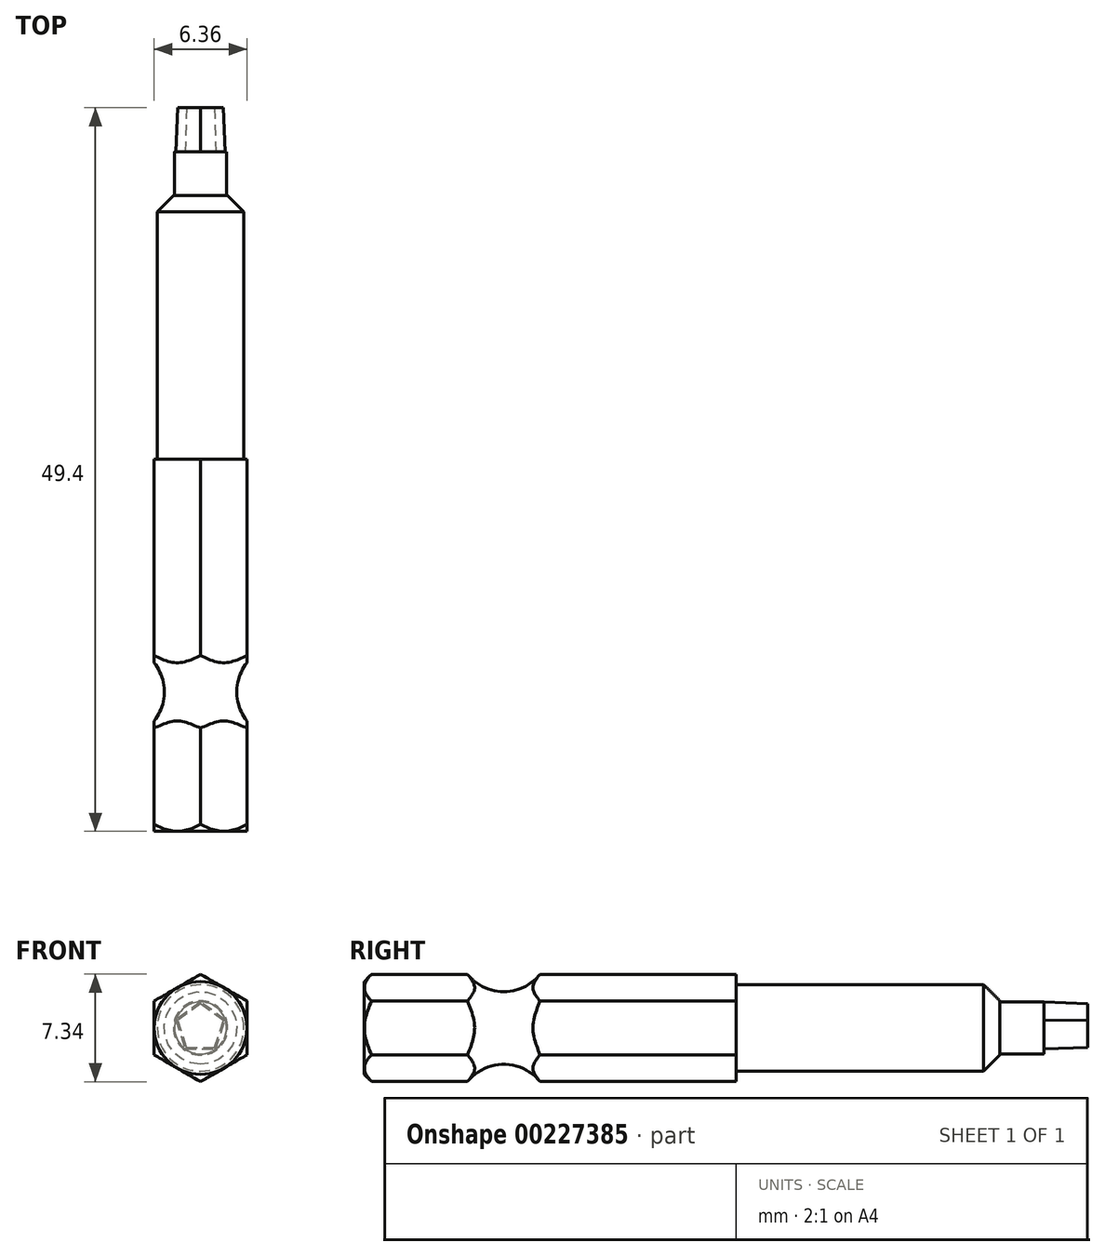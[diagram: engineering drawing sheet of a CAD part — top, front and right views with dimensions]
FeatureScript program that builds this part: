
annotation { "Feature Type Name" : "Feature", "Feature Type Description" : "" }
export const myFeature = defineFeature(function(context is Context, id is Id, definition is map)
    precondition{}
    {
        {
            var Q0;
            Q0=qCreatedBy(makeId("Front.planeOp"),FACE);
            var sketch = newSketch(context, id + "F0", { "sketchPlane" : qUnion([Q0])});
            skCircle(sketch, "E0.cCircle", {"center": v(0, 0) * mm, "radius": 3.17 * mm, "construction": true});
            skLineSegment(sketch, "E0.0", {"start": v(0, 3.67) * mm, "end": v(3.18, 1.83) * mm});
            skLineSegment(sketch, "E0.1", {"start": v(3.17, 1.83) * mm, "end": v(3.17, -1.83) * mm});
            skLineSegment(sketch, "E0.2", {"start": v(3.18, -1.83) * mm, "end": v(0, -3.67) * mm});
            skLineSegment(sketch, "E0.3", {"start": v(0, -3.67) * mm, "end": v(-3.17, -1.83) * mm});
            skLineSegment(sketch, "E0.4", {"start": v(-3.17, -1.83) * mm, "end": v(-3.17, 1.83) * mm});
            skLineSegment(sketch, "E0.5", {"start": v(-3.17, 1.83) * mm, "end": v(0, 3.67) * mm});
            skPoint(sketch, "E0.0.midPoint", {"position": v(1.59, 2.75) * mm});
            skSolve(sketch);
        }
        {
            var Q0;
            Q0=qSketchRegion(id+"F0",true);
            extrude(context, id + "F1", {"entities" : qUnion([Q0]), "oppositeDirection" : true, "depth" : 25.4 * mm});
        }
        {
            var Q0;
            Q0=qCreatedBy(makeId("Right.planeOp"),FACE);
            var sketch = newSketch(context, id + "F2", { "sketchPlane" : qUnion([Q0])});
            skLineSegment(sketch, "E1", {"start": v(0, 0) * mm, "end": v(2.72, 0) * mm});
            skSolve(sketch);
        }
        {
            var Q0;
            Q0=qCreatedBy(makeId("Right.planeOp"),FACE);
            var sketch = newSketch(context, id + "F3", { "sketchPlane" : qUnion([Q0])});
            skLineSegment(sketch, "E2", {"start": v(0, 3.67) * mm, "end": v(0.5, 3.67) * mm});
            skLineSegment(sketch, "E3", {"start": v(0.5, 3.67) * mm, "end": v(0, 3.17) * mm});
            skLineSegment(sketch, "E4", {"start": v(0, 3.17) * mm, "end": v(0, 3.67) * mm});
            skSolve(sketch);
        }
        {
            var Q0;
            Q0=qSketchRegion(id+"F3",true);
            var Q1;
            Q1=sQuery(id+"F2.wireOp",EDGE,"E1");
            revolve(context, id + "F4", {"operationType" : NewBodyOperationType.REMOVE, "entities" : qUnion([Q0]), "axis" : qUnion([Q1]), "revolveType" : RevolveType.FULL, "oppositeDirection" : true});
        }
        {
            var Q0;
            Q0=makeQuery(id+"F1.opExtrude","SWEPT_FACE",FACE,{"disambiguationData":[OSD([sQuery(id+"F0.wireOp",EDGE,"E0.0")])]});
            var sketch = newSketch(context, id + "F5", { "sketchPlane" : qUnion([Q0])});
            skPoint(sketch, "E5", {"position": v(0, 25.4) * mm});
            skSolve(sketch);
        }
        {
            var Q0;
            Q0=makeQuery(id+"F1.opExtrude","CAP_EDGE",EDGE,{"disambiguationData":[OSD([sQuery(id+"F0.wireOp",EDGE,"E0.0")])],"isStart":false});
            var Q1;
            Q1=sQuery(id+"F2.wireOp",VERTEX,"E1.start");
            cPlane(context, id + "F6", {"entities" : qUnion([Q0, Q1]), "cplaneType" : CPlaneType.LINE_POINT, "offset" : 150 * mm, "width" : 150 * mm, "height" : 150 * mm});
        }
        {
            var Q0;
            Q0=qCreatedBy(id+"F6.planeOp",FACE);
            var sketch = newSketch(context, id + "F7", { "sketchPlane" : qUnion([Q0])});
            skArc(sketch, "E6", {"start": v(6.41, 5.03) * mm, "mid": v(9.53, 2.48) * mm, "end": v(12.64, 5.03) * mm});
            skLineSegment(sketch, "E7", {"start": v(6.41, 5.03) * mm, "end": v(12.64, 5.03) * mm});
            skPoint(sketch, "E8", {"position": v(9.53, 2.48) * mm});
            skSolve(sketch);
        }
        {
            var Q0;
            Q0=qSketchRegion(id+"F7",true);
            var Q1;
            Q1=sQuery(id+"F2.wireOp",EDGE,"E1");
            revolve(context, id + "F8", {"operationType" : NewBodyOperationType.REMOVE, "entities" : qUnion([Q0]), "axis" : qUnion([Q1]), "revolveType" : RevolveType.FULL});
        }
        {
            var Q0;
            Q0=makeQuery(id+"F1.opExtrude","CAP_FACE",FACE,{"disambiguationData":[OSD([sQuery(id+"F0.wireOp",EDGE,"E0.0"),sQuery(id+"F0.wireOp",EDGE,"E0.1"),sQuery(id+"F0.wireOp",EDGE,"E0.2"),sQuery(id+"F0.wireOp",EDGE,"E0.3"),sQuery(id+"F0.wireOp",EDGE,"E0.4"),sQuery(id+"F0.wireOp",EDGE,"E0.5")])],"isStart":false});
            var sketch = newSketch(context, id + "F9", { "sketchPlane" : qUnion([Q0])});
            skCircle(sketch, "E9", {"center": v(0, 0) * mm, "radius": 2.95 * mm});
            skSolve(sketch);
        }
        {
            var Q0;
            Q0 = qSketchRegion(id + "F9", true);
            extrude(context, id + "F10", {"entities" : qUnion([Q0]), "operationType" : NewBodyOperationType.ADD, "depth" : 18 * mm, "offsetDistance" : 25 * mm});
        }
        {
            var Q0;
            Q0=makeQuery(id+"F10.opExtrude","CAP_FACE",FACE,{"disambiguationData":[OSD([sQuery(id+"F9.wireOp",EDGE,"E9")])],"isStart":false});
            var sketch = newSketch(context, id + "F11", { "sketchPlane" : qUnion([Q0])});
            skCircle(sketch, "E10", {"center": v(0, 0) * mm, "radius": 1.77 * mm});
            skSolve(sketch);
        }
        {
            var Q0;
            Q0 = qSketchRegion(id + "F11", true);
            extrude(context, id + "F12", {"entities" : qUnion([Q0]), "operationType" : NewBodyOperationType.ADD, "depth" : 3 * mm, "offsetDistance" : 25 * mm});
        }
        {
            var Q0;
            Q0=makeQuery(id+"F12.opExtrude","CAP_FACE",FACE,{"disambiguationData":[OSD([sQuery(id+"F11.wireOp",EDGE,"E10")])],"isStart":false});
            var sketch = newSketch(context, id + "F13", { "sketchPlane" : qUnion([Q0])});
            skCircle(sketch, "E11.cCircle", {"center": v(0, 0) * mm, "radius": 1.44 * mm, "construction": true});
            skLineSegment(sketch, "E11.0", {"start": v(0, 1.77) * mm, "end": v(1.69, 0.55) * mm});
            skLineSegment(sketch, "E11.1", {"start": v(1.69, 0.55) * mm, "end": v(1.04, -1.44) * mm});
            skLineSegment(sketch, "E11.2", {"start": v(1.04, -1.44) * mm, "end": v(-1.04, -1.44) * mm});
            skLineSegment(sketch, "E11.3", {"start": v(-1.04, -1.44) * mm, "end": v(-1.69, 0.55) * mm});
            skLineSegment(sketch, "E11.4", {"start": v(-1.69, 0.55) * mm, "end": v(0, 1.77) * mm});
            skPoint(sketch, "E11.0.midPoint", {"position": v(0.84, 1.16) * mm});
            skSolve(sketch);
        }
        {
            var Q0;
            Q0 = qSketchRegion(id + "F13", true);
            extrude(context, id + "F14", {"entities" : qUnion([Q0]), "operationType" : NewBodyOperationType.ADD, "depth" : 3 * mm, "offsetDistance" : 25 * mm, "hasDraft" : true, "draftAngle" : 2 * degree, "draftPullDirection" : true});
        }
        {
            var Q0;
            Q0=makeQuery(id+"F1.opExtrude","CAP_FACE",FACE,{"disambiguationData":[OSD([sQuery(id+"F0.wireOp",EDGE,"E0.0"),sQuery(id+"F0.wireOp",EDGE,"E0.1"),sQuery(id+"F0.wireOp",EDGE,"E0.2"),sQuery(id+"F0.wireOp",EDGE,"E0.3"),sQuery(id+"F0.wireOp",EDGE,"E0.4"),sQuery(id+"F0.wireOp",EDGE,"E0.5")])],"isStart":true});
            var Q1;
            Q1=makeQuery(id+"F1.opExtrude","CAP_FACE",FACE,{"disambiguationData":[OSD([sQuery(id+"F0.wireOp",EDGE,"E0.0"),sQuery(id+"F0.wireOp",EDGE,"E0.1"),sQuery(id+"F0.wireOp",EDGE,"E0.2"),sQuery(id+"F0.wireOp",EDGE,"E0.3"),sQuery(id+"F0.wireOp",EDGE,"E0.4"),sQuery(id+"F0.wireOp",EDGE,"E0.5")])],"isStart":false});
            cPlane(context, id + "F15", {"entities" : qUnion([Q0, Q1]), "cplaneType" : CPlaneType.MID_PLANE, "offset" : 25 * mm, "width" : 150 * mm, "height" : 150 * mm});
        }
        {
            var Q0;
            Q0=makeQuery(id+"F10.opExtrude","CAP_EDGE",EDGE,{"disambiguationData":[OSD([sQuery(id+"F9.wireOp",EDGE,"E9")])],"isStart":false});
            chamfer(context, id + "F16", {"entities" : qUnion([Q0]), "width" : 1.1 * mm, "tangentPropagation" : true});
        }
    });
